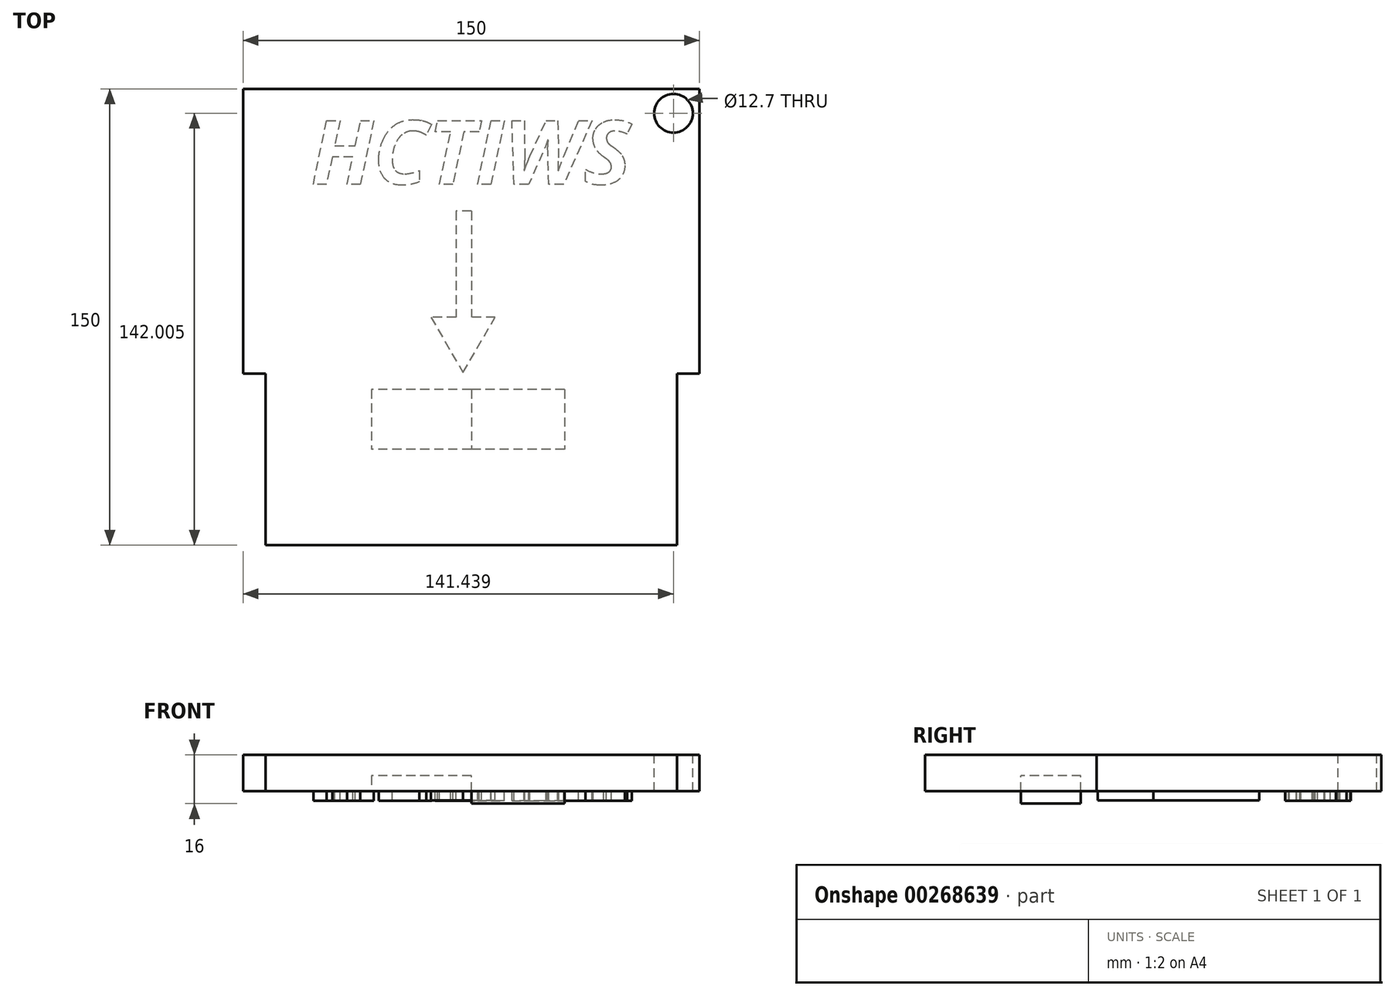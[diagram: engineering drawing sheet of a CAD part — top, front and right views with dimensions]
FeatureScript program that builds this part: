
annotation { "Feature Type Name" : "Feature", "Feature Type Description" : "" }
export const myFeature = defineFeature(function(context is Context, id is Id, definition is map)
    precondition{}
    {
        {
            var Q0;
            Q0=qCreatedBy(makeId("Top.planeOp"),FACE);
            var sketch = newSketch(context, id + "F0", { "sketchPlane" : qUnion([Q0])});
            skLineSegment(sketch, "E0.bottom", {"start": v(67.63, -75) * mm, "end": v(-67.63, -75) * mm});
            skLineSegment(sketch, "E0.top", {"start": v(75, 75) * mm, "end": v(-75, 75) * mm});
            skLineSegment(sketch, "E0.left", {"start": v(75, -18.66) * mm, "end": v(75, 75) * mm});
            skLineSegment(sketch, "E0.right", {"start": v(-75, -18.66) * mm, "end": v(-75, 75) * mm});
            skPoint(sketch, "E0.middle", {"position": v(0, 0) * mm});
            skLineSegment(sketch, "E1", {"start": v(-75, -18.66) * mm, "end": v(-67.63, -18.66) * mm});
            skLineSegment(sketch, "E2", {"start": v(-67.63, -18.66) * mm, "end": v(-67.63, -75) * mm});
            skLineSegment(sketch, "E3", {"start": v(67.63, -18.66) * mm, "end": v(75, -18.66) * mm});
            skLineSegment(sketch, "E4", {"start": v(67.63, -18.66) * mm, "end": v(67.63, -75) * mm});
            skSolve(sketch);
        }
        {
            var Q0;
            Q0=makeQuery(id+"F0.imprint","IMPRINT",FACE,{"disambiguationData":[TD([[makeQuery(id+"F0.imprint","IMPRINT",EDGE,{"derivedFrom":sQuery(id+"F0.wireOp",EDGE,"E0.bottom")}),-1.0]])]});
            extrude(context, id + "F1", {"entities" : qUnion([Q0]), "depth" : 11.94 * mm});
        }
        {
            var Q0;
            Q0=makeQuery(id+"F1.opExtrude","CAP_FACE",FACE,{"disambiguationData":[OSD([sQuery(id+"F0.wireOp",EDGE,"E0.bottom"),sQuery(id+"F0.wireOp",EDGE,"E0.top"),sQuery(id+"F0.wireOp",EDGE,"E0.left"),sQuery(id+"F0.wireOp",EDGE,"E0.right"),sQuery(id+"F0.wireOp",EDGE,"E1"),sQuery(id+"F0.wireOp",EDGE,"E2"),sQuery(id+"F0.wireOp",EDGE,"E3"),sQuery(id+"F0.wireOp",EDGE,"E4")])],"isStart":false});
            var sketch = newSketch(context, id + "F2", { "sketchPlane" : qUnion([Q0])});
            skCircle(sketch, "E5", {"center": v(66.44, 67) * mm, "radius": 6.35 * mm});
            skSolve(sketch);
        }
        {
            var Q0;
            Q0=makeQuery(id+"F2.imprint","IMPRINT",FACE,{"disambiguationData":[TD([[makeQuery(id+"F2.imprint","IMPRINT",EDGE,{"derivedFrom":sQuery(id+"F2.wireOp",EDGE,"E5")}),1.0]])]});
            extrude(context, id + "F3", {"entities" : qUnion([Q0]), "operationType" : NewBodyOperationType.REMOVE, "oppositeDirection" : true, "depth" : 25.4 * mm});
        }
        {
            var Q0;
            Q0=makeQuery(id+"F1.opExtrude","CAP_FACE",FACE,{"disambiguationData":[OSD([sQuery(id+"F0.wireOp",EDGE,"E0.bottom"),sQuery(id+"F0.wireOp",EDGE,"E0.top"),sQuery(id+"F0.wireOp",EDGE,"E0.left"),sQuery(id+"F0.wireOp",EDGE,"E0.right"),sQuery(id+"F0.wireOp",EDGE,"E1"),sQuery(id+"F0.wireOp",EDGE,"E2"),sQuery(id+"F0.wireOp",EDGE,"E3"),sQuery(id+"F0.wireOp",EDGE,"E4")])],"isStart":false});
            var sketch = newSketch(context, id + "F4", { "sketchPlane" : qUnion([Q0])});
            skText(sketch, "E6", { "text": "HCTIWS", "fontName": "OpenSans-BoldItalic.ttf"});
            const initialGuessF4  = {"E6": [-0.05272, 0.04365, 1, 0, 0.0211]};
            skSetInitialGuess(sketch, initialGuessF4);
            skSolve(sketch);
        }
        {
            var Q0;
            Q0 = qSketchRegion(id + "F4", true);
            extrude(context, id + "F5", {"entities" : qUnion([Q0]), "operationType" : NewBodyOperationType.ADD, "oppositeDirection" : true, "depth" : 15 * mm});
        }
        {
            var Q0;
            Q0=makeQuery(id+"F1.opExtrude","CAP_FACE",FACE,{"disambiguationData":[OSD([sQuery(id+"F0.wireOp",EDGE,"E0.bottom"),sQuery(id+"F0.wireOp",EDGE,"E0.top"),sQuery(id+"F0.wireOp",EDGE,"E0.left"),sQuery(id+"F0.wireOp",EDGE,"E0.right"),sQuery(id+"F0.wireOp",EDGE,"E1"),sQuery(id+"F0.wireOp",EDGE,"E2"),sQuery(id+"F0.wireOp",EDGE,"E3"),sQuery(id+"F0.wireOp",EDGE,"E4")])],"isStart":true});
            var sketch = newSketch(context, id + "F6", { "sketchPlane" : qUnion([Q0])});
            skLineSegment(sketch, "E7", {"start": v(0, -34.82) * mm, "end": v(0, 0) * mm});
            skLineSegment(sketch, "E8", {"start": v(0, -34.82) * mm, "end": v(-5.05, -34.82) * mm});
            skLineSegment(sketch, "E9", {"start": v(-5.05, -34.82) * mm, "end": v(-5.05, 0) * mm});
            skLineSegment(sketch, "E10.0", {"start": v(7.84, 0) * mm, "end": v(0, 0) * mm});
            skLineSegment(sketch, "E10.1", {"start": v(-13.27, 0) * mm, "end": v(-2.72, 18.28) * mm});
            skLineSegment(sketch, "E10.2", {"start": v(-2.72, 18.28) * mm, "end": v(7.84, 0) * mm});
            skLineSegment(sketch, "E11.trimOffspring", {"start": v(-5.05, 0) * mm, "end": v(-13.27, 0) * mm});
            skSolve(sketch);
        }
        {
            var Q0;
            Q0 = qSketchRegion(id + "F6", true);
            extrude(context, id + "F7", {"entities" : qUnion([Q0]), "operationType" : NewBodyOperationType.ADD, "depth" : 3.05 * mm});
        }
        {
            var Q0;
            Q0=makeQuery(id+"F1.opExtrude","CAP_FACE",FACE,{"disambiguationData":[OSD([sQuery(id+"F0.wireOp",EDGE,"E0.bottom"),sQuery(id+"F0.wireOp",EDGE,"E0.top"),sQuery(id+"F0.wireOp",EDGE,"E0.left"),sQuery(id+"F0.wireOp",EDGE,"E0.right"),sQuery(id+"F0.wireOp",EDGE,"E1"),sQuery(id+"F0.wireOp",EDGE,"E2"),sQuery(id+"F0.wireOp",EDGE,"E3"),sQuery(id+"F0.wireOp",EDGE,"E4")])],"isStart":true});
            var sketch = newSketch(context, id + "F8", { "sketchPlane" : qUnion([Q0])});
            skLineSegment(sketch, "E12.bottom", {"start": v(30.66, 23.83) * mm, "end": v(-32.84, 23.83) * mm});
            skLineSegment(sketch, "E12.top", {"start": v(30.66, 43.5) * mm, "end": v(-32.84, 43.5) * mm});
            skLineSegment(sketch, "E12.left", {"start": v(30.66, 23.83) * mm, "end": v(30.66, 43.5) * mm});
            skLineSegment(sketch, "E12.right", {"start": v(-32.84, 23.83) * mm, "end": v(-32.84, 43.5) * mm});
            skSolve(sketch);
        }
        {
            var Q0;
            Q0 = qSketchRegion(id + "F8", true);
            extrude(context, id + "F9", {"entities" : qUnion([Q0]), "operationType" : NewBodyOperationType.REMOVE, "oppositeDirection" : true, "depth" : 5.08 * mm});
        }
        {
            var Q0;
            Q0=makeQuery(id+"F9.boolean.opBoolean","COPY",FACE,{"derivedFrom":makeQuery(id+"F9.opExtrude","CAP_FACE",FACE,{"disambiguationData":[OSD([sQuery(id+"F8.wireOp",EDGE,"E12.bottom"),sQuery(id+"F8.wireOp",EDGE,"E12.top"),sQuery(id+"F8.wireOp",EDGE,"E12.left"),sQuery(id+"F8.wireOp",EDGE,"E12.right")])],"isStart":false})});
            var sketch = newSketch(context, id + "F10", { "sketchPlane" : qUnion([Q0])});
            skLineSegment(sketch, "E13.bottom", {"start": v(30.66, 23.83) * mm, "end": v(0, 23.83) * mm});
            skLineSegment(sketch, "E13.top", {"start": v(30.66, 43.5) * mm, "end": v(0, 43.5) * mm});
            skLineSegment(sketch, "E13.left", {"start": v(30.66, 23.83) * mm, "end": v(30.66, 43.5) * mm});
            skLineSegment(sketch, "E13.right", {"start": v(0, 23.83) * mm, "end": v(0, 43.5) * mm});
            skSolve(sketch);
        }
        {
            var Q0;
            Q0 = qSketchRegion(id + "F10", true);
            extrude(context, id + "F11", {"entities" : qUnion([Q0]), "operationType" : NewBodyOperationType.ADD, "depth" : 9.14 * mm});
        }
    });
